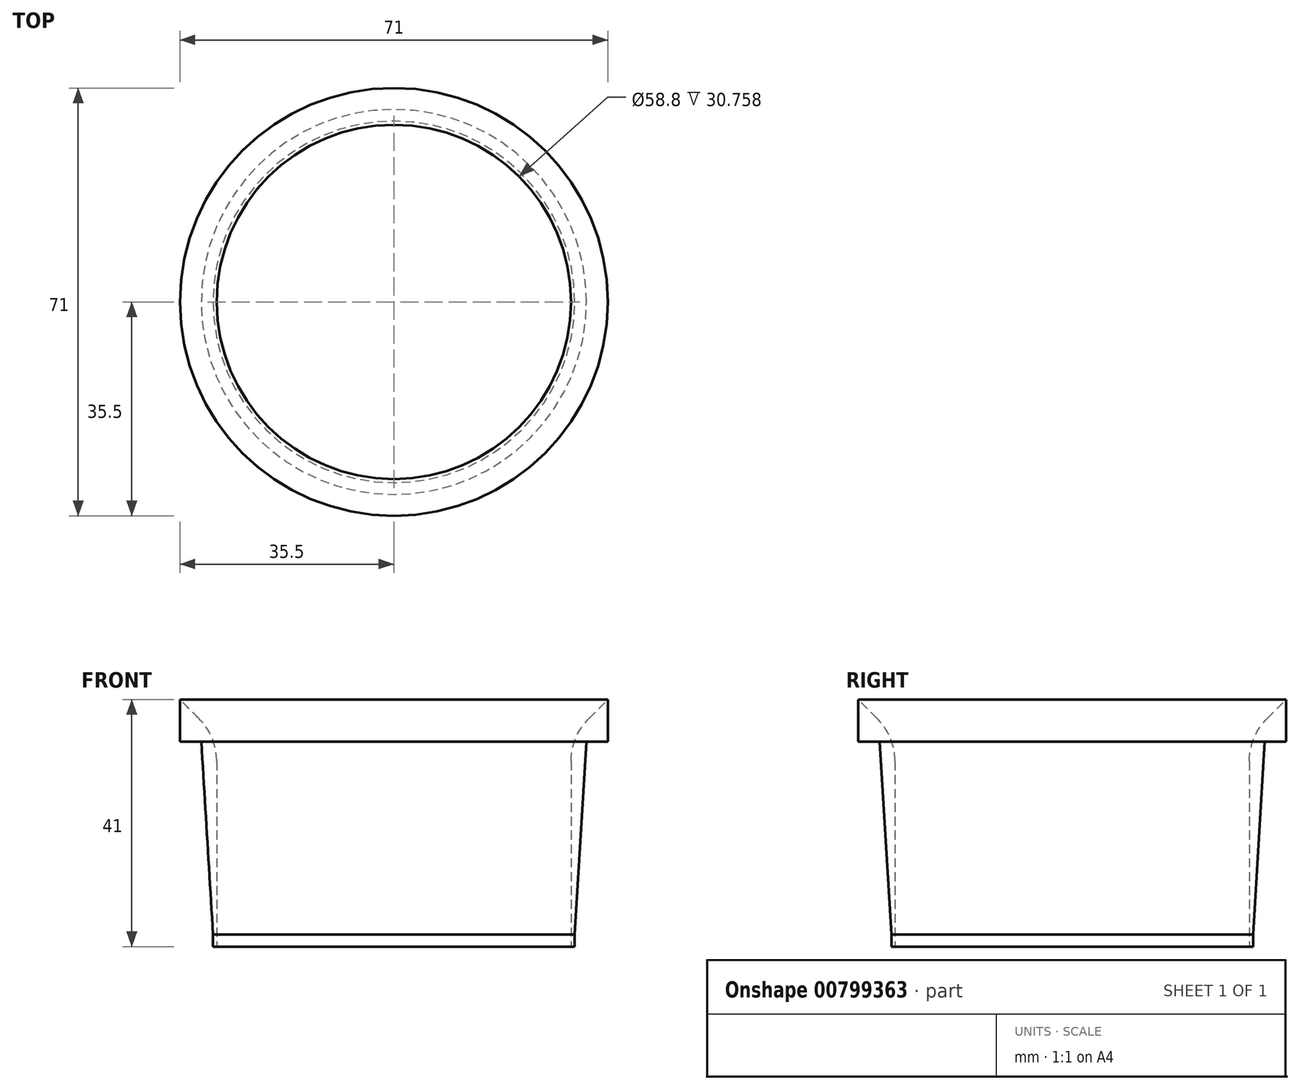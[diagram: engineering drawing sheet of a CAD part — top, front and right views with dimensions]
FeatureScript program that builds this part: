
annotation { "Feature Type Name" : "Feature", "Feature Type Description" : "" }
export const myFeature = defineFeature(function(context is Context, id is Id, definition is map)
    precondition{}
    {
        {
            var Q0;
            Q0=qCreatedBy(makeId("Front.planeOp"),FACE);
            var sketch = newSketch(context, id + "F0", { "sketchPlane" : qUnion([Q0])});
            skLineSegment(sketch, "E0", {"start": v(0, 36) * mm, "end": v(31.98, 36) * mm});
            skLineSegment(sketch, "E1", {"start": v(31.98, 36) * mm, "end": v(30.2, 0) * mm});
            skLineSegment(sketch, "E2", {"start": v(30.2, 0) * mm, "end": v(0, 0) * mm});
            skSolve(sketch);
        }
        {
            var Q0;
            Q0=qCreatedBy(makeId("Front.planeOp"),FACE);
            var sketch = newSketch(context, id + "F1", { "sketchPlane" : qUnion([Q0])});
            skLineSegment(sketch, "E3", {"start": v(35.5, 36) * mm, "end": v(35.5, 43) * mm});
            skLineSegment(sketch, "E4", {"start": v(35.5, 36) * mm, "end": v(31.95, 36) * mm});
            skLineSegment(sketch, "E5", {"start": v(31.95, 36) * mm, "end": v(30, 4) * mm});
            skLineSegment(sketch, "E6", {"start": v(30, 4) * mm, "end": v(30, 2) * mm});
            skLineSegment(sketch, "E7", {"start": v(30, 2) * mm, "end": v(29.4, 2) * mm});
            skLineSegment(sketch, "E8", {"start": v(29.4, 2) * mm, "end": v(29.4, 4) * mm});
            skLineSegment(sketch, "E9", {"start": v(29.4, 4) * mm, "end": v(29.4, 32.76) * mm});
            skLineSegment(sketch, "E10", {"start": v(32.33, 39.83) * mm, "end": v(35.5, 43) * mm});
            skPoint(sketch, "E11.visualSharp", {"position": v(29.4, 36.9) * mm});
            skArc(sketch, "E11.filletArc", {"start": v(32.33, 39.83) * mm, "mid": v(30.16, 36.58) * mm, "end": v(29.4, 32.76) * mm});
            skSolve(sketch);
        }
        {
            var Q0;
            Q0=qCreatedBy(makeId("Front.planeOp"),FACE);
            var sketch = newSketch(context, id + "F2", { "sketchPlane" : qUnion([Q0])});
            skLineSegment(sketch, "E12", {"start": v(0, -21.5) * mm, "end": v(0, 51.65) * mm});
            skSolve(sketch);
        }
        {
            var Q0;
            Q0=makeQuery(id+"F1.imprint","IMPRINT",FACE,{"disambiguationData":[TD([[makeQuery(id+"F1.imprint","IMPRINT",EDGE,{"derivedFrom":sQuery(id+"F1.wireOp",EDGE,"E3")}),1.0]])]});
            var Q1;
            Q1=sQuery(id+"F2.wireOp",EDGE,"E12");
            revolve(context, id + "F3", {"surfaceOperationType" : NewSurfaceOperationType.NEW, "entities" : qUnion([Q0]), "axis" : qUnion([Q1]), "revolveType" : RevolveType.FULL});
        }
    });
